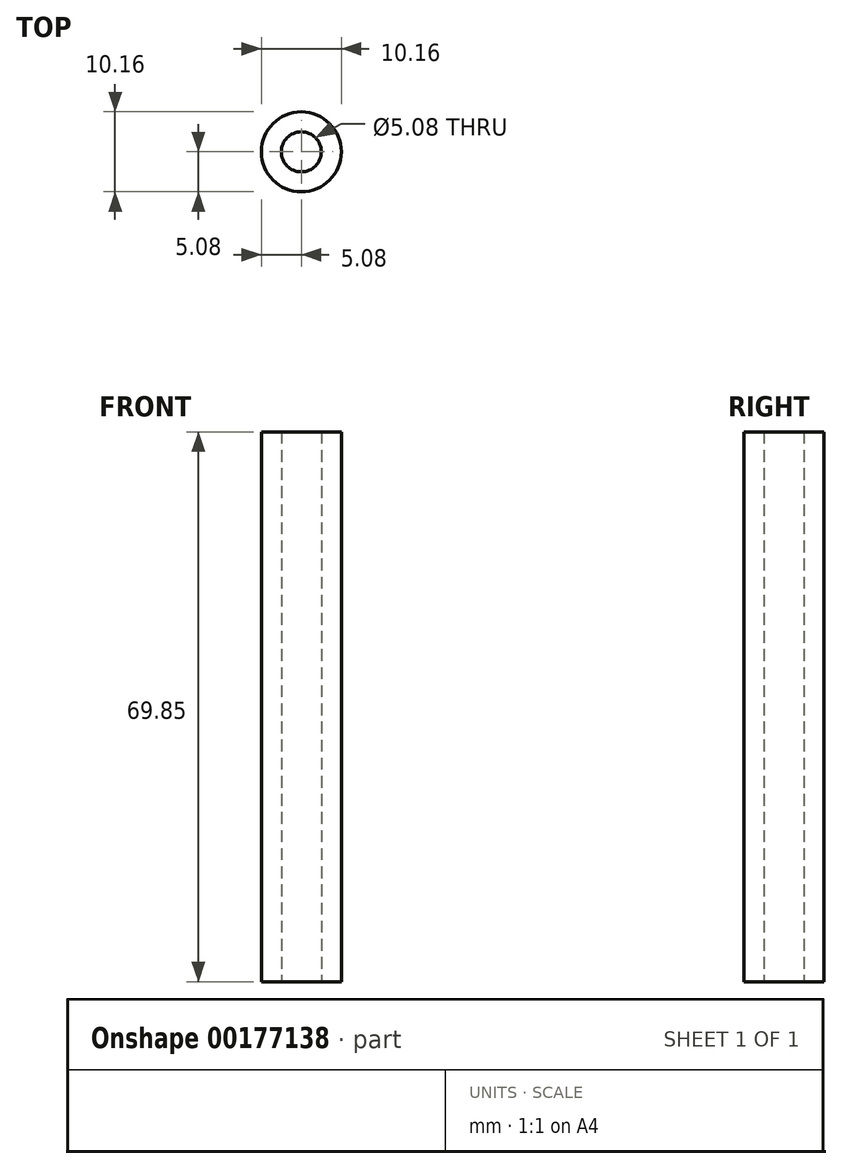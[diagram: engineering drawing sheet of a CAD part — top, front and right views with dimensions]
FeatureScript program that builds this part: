
annotation { "Feature Type Name" : "Feature", "Feature Type Description" : "" }
export const myFeature = defineFeature(function(context is Context, id is Id, definition is map)
    precondition{}
    {
        {
            var Q0;
            Q0=qCreatedBy(makeId("Top.planeOp"),FACE);
            var sketch = newSketch(context, id + "F0", { "sketchPlane" : qUnion([Q0])});
            skCircle(sketch, "E0", {"center": v(0, 0) * mm, "radius": 5.08 * mm});
            skCircle(sketch, "E1", {"center": v(0, 0) * mm, "radius": 2.54 * mm});
            skSolve(sketch);
        }
        {
            var Q0;
            Q0 = qSketchRegion(id + "F0", true);
            extrude(context, id + "F1", {"entities" : qUnion([Q0]), "depth" : 69.85 * mm});
        }
    });
